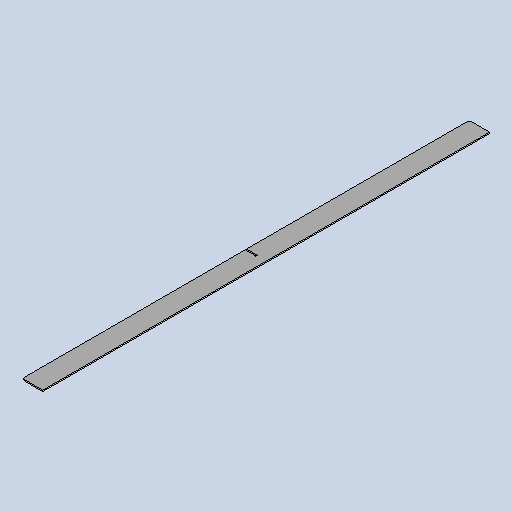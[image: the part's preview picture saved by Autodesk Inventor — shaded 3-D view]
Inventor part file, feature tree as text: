
AUTODESK INVENTOR PART (.ipt)
format: ipt  version: 2025 (Build 290162010, 162A)  size: 273,408 bytes
history: native  units: mm
features: sheet_metal_op x1, chamfer x1, sketch x1, other x1
ambient origin geometry x8: Origin, YZ Plane, XZ Plane, XY Plane, X Axis, Y Axis, Z Axis, Center Point
bodies: Body1 (feature_tree)
feature tree (4):
  sheet_metal_op  "Face2"
  chamfer  "Corner Round1"
  sketch  "Sketch1"  dims[d15=3.0mm d17=1098.0mm d18=50.0mm d19=3.0mm d20=26.0mm d21=6.0mm]
  other  "Plate2"
